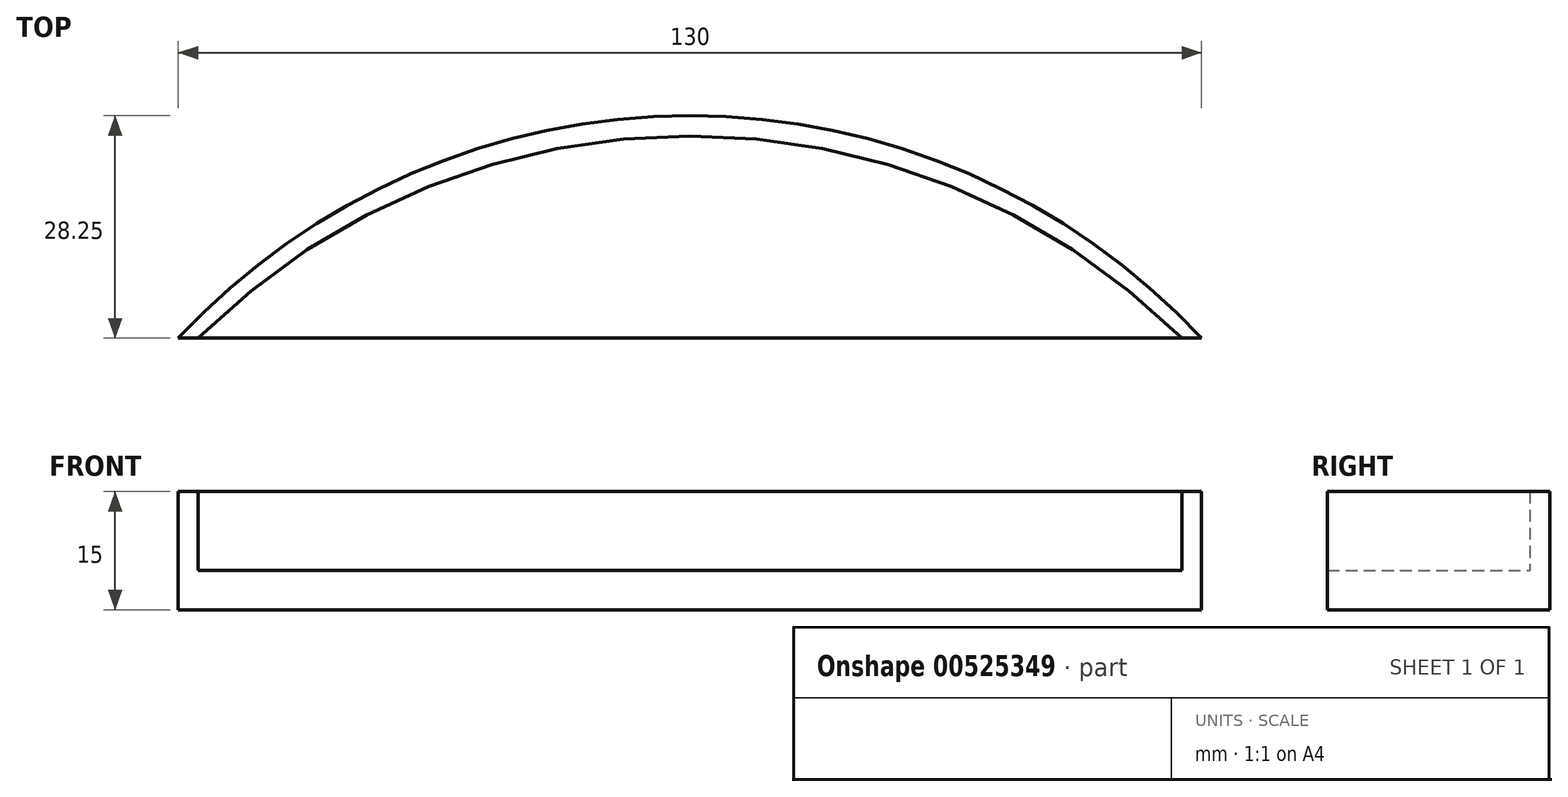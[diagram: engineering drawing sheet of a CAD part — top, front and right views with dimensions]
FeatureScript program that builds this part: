
annotation { "Feature Type Name" : "Feature", "Feature Type Description" : "" }
export const myFeature = defineFeature(function(context is Context, id is Id, definition is map)
    precondition{}
    {
        {
            var Q0;
            Q0=qCreatedBy(makeId("Top.planeOp"),FACE);
            var sketch = newSketch(context, id + "F0", { "sketchPlane" : qUnion([Q0])});
            skCircle(sketch, "E0", {"center": v(0, 0) * mm, "radius": 88.9 * mm});
            skLineSegment(sketch, "E1", {"start": v(-65, 60.65) * mm, "end": v(65, 60.65) * mm});
            skSolve(sketch);
        }
        {
            var Q0;
            {var subQ0=sQuery(id+"F0.wireOp",EDGE,"E1");Q0=makeQuery(id+"F0.imprint","IMPRINT",FACE,{"disambiguationData":[TD([[makeQuery(id+"F0.imprint","IMPRINT",EDGE,{"derivedFrom":subQ0}),1.0]])]});}
            extrude(context, id + "F1", {"entities" : qUnion([Q0]), "depth" : 5 * mm, "offsetDistance" : 25 * mm});
        }
        {
            var Q0;
            Q0=makeQuery(id+"F1.opExtrude","CAP_FACE",FACE,{"disambiguationData":[OSD([sQuery(id+"F0.wireOp",EDGE,"E0"),sQuery(id+"F0.wireOp",EDGE,"E1")])],"isStart":false});
            var sketch = newSketch(context, id + "F2", { "sketchPlane" : qUnion([Q0])});
            skArc(sketch, "E2", {"start": v(62.5, 60.65) * mm, "mid": v(0, 86.33) * mm, "end": v(-62.5, 60.65) * mm});
            skLineSegment(sketch, "E3", {"start": v(-65, 60.65) * mm, "end": v(-62.5, 60.65) * mm});
            skLineSegment(sketch, "E4", {"start": v(62.5, 60.65) * mm, "end": v(65, 60.65) * mm});
            skArc(sketch, "E5.0", {"start": v(65, 60.65) * mm, "mid": v(0, 88.9) * mm, "end": v(-65, 60.65) * mm});
            skSolve(sketch);
        }
        {
            var Q0;
            Q0 = qSketchRegion(id + "F2", true);
            extrude(context, id + "F3", {"entities" : qUnion([Q0]), "operationType" : NewBodyOperationType.ADD, "depth" : 10 * mm, "offsetDistance" : 25 * mm});
        }
    });
